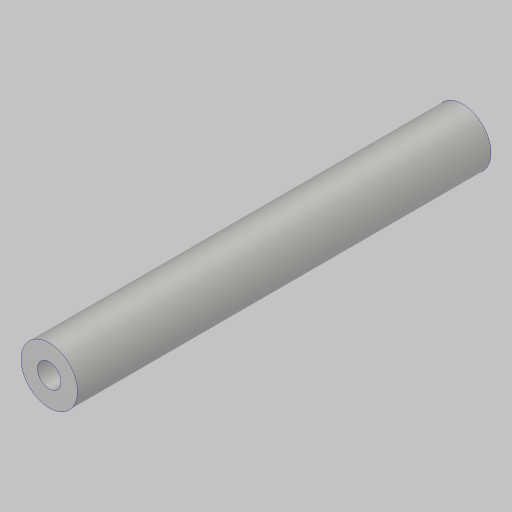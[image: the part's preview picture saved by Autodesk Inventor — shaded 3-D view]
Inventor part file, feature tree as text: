
AUTODESK INVENTOR PART (.ipt)
format: ipt  version: 2023.5 (Build 275446000, 446)  size: 110,592 bytes
history: native  units: in
note: dims shown in document units (in); Inventor stores cm internally (conversion verified against a paired STEP export)
features: extrude x1, hole x1
ambient origin geometry x8: Origin, YZ Plane, XZ Plane, XY Plane, X Axis, Y Axis, Z Axis, Center Point
bodies: Solid1 (feature_tree)
feature tree (2):
  extrude  "Extrusion1"  Depth=2.75in
  hole  "Hole1"  [1 undecoded]
note: 1 required parameter value undecoded (feature->parameter linkage not recoverable at this tier; creation-order binding heuristic only, values carry confidence <= 0.55)
